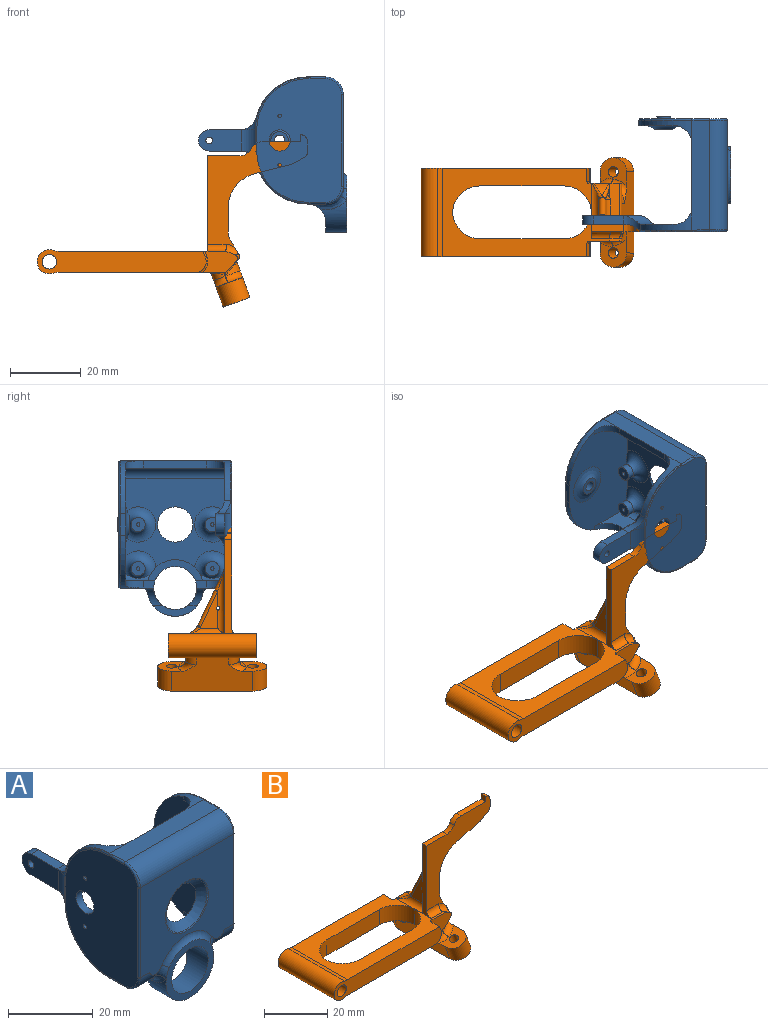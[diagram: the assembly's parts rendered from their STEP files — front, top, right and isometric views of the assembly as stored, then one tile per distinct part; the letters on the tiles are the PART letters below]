
ASSEMBLY  parts=2 mates=1
PART A: 112 faces, bbox 37.6x43.4x49.7 mm
  f0: plane 34.28x22.36mm, normal (1,0,0), area 579.8mm2, adj f18,f21,f30,f32,f33,f34,f36,f37
  f1: cylinder r=5mm len=6.53mm, axis (1,0,0), area 41.7mm2, adj f8,f9,f23,f66,f86,f87
  f2: cylinder r=5mm len=0.6mm, axis (1,0,0), area 0.1mm2, adj f9,f39,f89
  f3: plane 7.91x5.41mm, normal (0,0,-1), area 34.3mm2, adj f6,f20,f28,f70,f90
  f4: plane 3.24x2mm, normal (0,1,0), area 6mm2, adj f23,f30,f36,f80,f92
  f5: plane 10x8.24mm, normal (0,0,1), area 46.6mm2, adj f7,f28,f31,f35,f80,f82
  f6: cylinder r=5mm len=6.53mm, axis (1,0,0), area 41.7mm2, adj f3,f9,f39,f68,f89,f90
  f7: cylinder r=3mm len=6.99mm, axis (1,0,0), area 18.7mm2, adj f5,f31,f53,f81
  f8: cylinder r=2mm len=3.87mm, axis (0,1,0), area 0.6mm2, adj f1,f9,f44,f87
  f9: plane 31x27.5mm, normal (0,-1,0), area 595.5mm2, adj f1,f2,f6,f8,f27,f39,f44,f55
  f10: plane 1x1mm, normal (0,1,0), area 0.8mm2, adj f43
  f11: cylinder r=0.5mm len=5mm, axis (0,1,0), area 15.7mm2, adj f13,f40
  f12: cylinder r=2mm len=4mm, axis (0,1,0), area 25.1mm2, adj f13,f52
  f13: plane 4x4mm, normal (0,1,0), area 11.8mm2, adj f11,f12
  f14: plane 1x1mm, normal (0,1,0), area 0.8mm2, adj f17
  f15: cylinder r=2mm len=4mm, axis (0,1,0), area 25.1mm2, adj f16,f53
  f16: plane 4x4mm, normal (0,1,0), area 11.8mm2, adj f15,f17
  f17: cylinder r=0.5mm len=5mm, axis (0,1,0), area 15.7mm2, adj f14,f16
  f18: cylinder r=15mm len=14.52mm, axis (1,0,0), area 38.7mm2, adj f0,f25,f37,f97,f102,f103
  f19: cylinder r=15mm len=15mm, axis (1,0,0), area 40.7mm2, adj f25,f26,f31,f38,f73
  f20: cylinder r=15mm len=15mm, axis (-1,0,0), area 40.7mm2, adj f3,f26,f31,f35,f72
  f21: cylinder r=15mm len=14.52mm, axis (-1,0,0), area 38.7mm2, adj f0,f23,f36,f99,f100,f101
  f22: plane 35x24mm, normal (-1,0,0), area 711.2mm2, adj f56,f57,f58,f59,f60,f61,f62,f63
  f23: plane 8.1x5.41mm, normal (0,0,-1), area 34.6mm2, adj f1,f4,f21,f64,f86,f99
  f24: plane 35x24mm, normal (1,0,0), area 728.5mm2, adj f67,f68,f69,f70,f71,f72,f73,f74
  f25: plane 31.21x5.03mm, normal (0,0,1), area 155.3mm2, adj f18,f19,f27,f29,f61,f71,f97
  f26: plane 6x1.5mm, normal (0,1,0), area 9mm2, adj f19,f20,f31,f74
  f27: cylinder r=5mm len=31mm, axis (-1,0,0), area 243.5mm2, adj f9,f25,f63,f69
  f28: plane 3.24x2mm, normal (0,1,0), area 6mm2, adj f3,f5,f35,f80,f91
  f29: plane 18x2mm, normal (0,1,0), area 36mm2, adj f25,f32,f37,f38
  f30: plane 10x8.24mm, normal (0,0,1), area 46.6mm2, adj f0,f4,f36,f45,f80,f82
  f31: plane 34.28x23mm, normal (-1,0,0), area 580.8mm2, adj f5,f7,f19,f20,f26,f32,f33,f34
  f32: plane 28x10mm, normal (0,0,-1), area 150.7mm2, adj f0,f29,f31,f34,f37,f38
  f33: plane 28x25.2mm, normal (0,1,0), area 402mm2, adj f0,f31,f34,f50,f51,f52,f53,f54
  f34: cylinder r=3mm len=28mm, axis (-1,0,0), area 131.9mm2, adj f0,f31,f32,f33
  f35: cylinder r=5mm len=5mm, axis (0,0,-1), area 12.3mm2, adj f5,f20,f28,f31
  f36: cylinder r=5mm len=5mm, axis (0,0,1), area 12.3mm2, adj f0,f4,f21,f30
  f37: cylinder r=5mm len=5mm, axis (0,0,1), area 12.3mm2, adj f0,f18,f29,f32
  f38: cylinder r=5mm len=5mm, axis (0,0,-1), area 12.3mm2, adj f19,f29,f31,f32
  f39: cylinder r=2mm len=3.87mm, axis (0,1,0), area 0.6mm2, adj f2,f6,f9,f89
  f40: plane 1x1mm, normal (0,1,0), area 0.8mm2, adj f11
  f41: plane 4x4mm, normal (0,1,0), area 11.8mm2, adj f42,f43
  f42: cylinder r=2mm len=4mm, axis (0,1,0), area 25.1mm2, adj f41,f51
  f43: cylinder r=0.5mm len=5mm, axis (0,1,0), area 15.7mm2, adj f10,f41
  f44: cylinder r=5mm len=0.6mm, axis (1,0,0), area 0.1mm2, adj f8,f9,f87
  f45: cylinder r=3mm len=6.99mm, axis (1,0,0), area 18.7mm2, adj f0,f30,f50,f81
  f46: cylinder r=0.5mm len=5mm, axis (0,1,0), area 15.7mm2, adj f47,f49
  f47: plane 4x4mm, normal (0,1,0), area 11.8mm2, adj f46,f48
  f48: cylinder r=2mm len=4mm, axis (0,1,0), area 25.1mm2, adj f47,f50
  f49: plane 1x1mm, normal (0,1,0), area 0.8mm2, adj f46
  f50: torus R=5mm, axis (0,-1,0), area 66.5mm2, adj f0,f33,f45,f48,f81
  f51: torus R=5mm, axis (0,-1,0), area 83.9mm2, adj f0,f33,f42
  f52: torus R=5mm, axis (0,-1,0), area 83.9mm2, adj f12,f31,f33
  f53: torus R=5mm, axis (0,-1,0), area 66.5mm2, adj f7,f15,f31,f33,f81
  f54: cone r=5mm half-angle=45deg, axis (0,-1,0), area 97.6mm2, adj f33,f55
  f55: torus R=7.21mm, axis (0,-1,0), area 17.3mm2, adj f9,f54
  f56: cylinder r=3mm len=6mm, axis (-1,0,0), area 37.7mm2, adj f0,f22,f107
  f57: cylinder r=0.5mm len=2mm, axis (-1,0,0), area 6.3mm2, adj f0,f22
  f58: cylinder r=0.5mm len=2mm, axis (-1,0,0), area 6.3mm2, adj f0,f22
  f59: torus R=14.5mm, axis (1,0,0), area 10.2mm2, adj f22,f60,f61,f97
  f60: cylinder r=0.5mm len=6mm, axis (0,0,1), area 2.6mm2, adj f22,f59,f62,f98
  f61: cylinder r=0.5mm len=5mm, axis (0,-1,0), area 3.5mm2, adj f22,f25,f59,f63,f97
  f62: torus R=14.5mm, axis (1,0,0), area 10.2mm2, adj f22,f60,f64,f99
  f63: torus R=4.5mm, axis (1,0,0), area 5.9mm2, adj f22,f27,f61,f65
  f64: cylinder r=0.5mm len=5mm, axis (0,1,0), area 3.5mm2, adj f22,f23,f62,f66,f99
  f65: cylinder r=0.5mm len=26mm, axis (0,0,-1), area 20.4mm2, adj f9,f22,f63,f66
  f66: torus R=4.5mm, axis (1,0,0), area 5.9mm2, adj f1,f22,f64,f65
  f67: cylinder r=0.5mm len=26mm, axis (0,0,1), area 20.4mm2, adj f9,f24,f68,f69
  f68: torus R=4.5mm, axis (1,0,0), area 5.9mm2, adj f6,f24,f67,f70
  f69: torus R=4.5mm, axis (1,0,0), area 5.9mm2, adj f24,f27,f67,f71
  f70: cylinder r=0.5mm len=5mm, axis (0,-1,0), area 3.9mm2, adj f3,f24,f68,f72
  f71: cylinder r=0.5mm len=5mm, axis (0,1,0), area 3.9mm2, adj f24,f25,f69,f73
  f72: torus R=14.5mm, axis (1,0,0), area 18.3mm2, adj f20,f24,f70,f74
  f73: torus R=14.5mm, axis (1,0,0), area 18.3mm2, adj f19,f24,f71,f74
  f74: cylinder r=0.5mm len=6mm, axis (0,0,-1), area 4.7mm2, adj f24,f26,f72,f73
  f75: cylinder r=1.5mm len=3.5mm, axis (1,0,0), area 33mm2, adj f76,f79
  f76: plane 5x5mm, normal (-1,0,0), area 12.6mm2, adj f75,f77
  f77: torus R=5.5mm, axis (1,0,0), area 79.8mm2, adj f31,f76
  f78: cylinder r=2mm len=4mm, axis (-1,0,0), area 6.3mm2, adj f24,f79
  f79: plane 4x4mm, normal (1,0,0), area 5.5mm2, adj f75,f78
  f80: cylinder r=6.1mm len=12.2mm, axis (0,-1,0), area 261.4mm2, adj f4,f5,f28,f30,f82,f83,f84,f91
  f81: cylinder r=8mm len=15.49mm, axis (0,-1,0), area 56.2mm2, adj f7,f33,f45,f50,f53,f82
  f82: plane 15.49x6mm, normal (0,1,0), area 34.4mm2, adj f5,f30,f80,f81
  f83: plane 12.49x3mm, normal (0,1,0), area 20.9mm2, adj f80,f85,f91,f92
  f84: plane 16.13x16.13mm, normal (0,-1,0), area 84.2mm2, adj f80,f85,f87,f88,f89
  f85: cylinder r=8mm len=16mm, axis (0,-1,0), area 146.5mm2, adj f83,f84,f86,f90,f91,f92
  f86: bspline ~11.94x4.3mm, area 23.5mm2, adj f1,f23,f85,f87,f92
  f87: bspline ~4.41x3.22mm, area 7.4mm2, adj f1,f8,f44,f84,f86,f88
  f88: torus R=9.73mm, axis (0,-1,0), area 37.9mm2, adj f9,f84,f87,f89
  f89: bspline ~4.41x3.22mm, area 7.4mm2, adj f2,f6,f39,f84,f88,f90
  f90: bspline ~11.94x4.3mm, area 23.5mm2, adj f3,f6,f85,f89,f91
  f91: cylinder r=5mm len=5mm, axis (-1,0,0), area 15.1mm2, adj f28,f80,f83,f85,f90
  f92: cylinder r=5mm len=5mm, axis (1,0,0), area 15.1mm2, adj f4,f80,f83,f85,f86
  f93: plane 12.26x6.08mm, normal (-1,0,0), area 66.9mm2, adj f94,f95,f97,f98,f99,f101,f103,f104
  f94: plane 8.64x2.5mm, normal (0,0,1), area 21.6mm2, adj f93,f96,f103,f104
  f95: plane 8.64x2.5mm, normal (0,0,-1), area 21.6mm2, adj f93,f96,f101,f104
  f96: plane 15.91x6mm, normal (1,0,0), area 88.5mm2, adj f94,f95,f100,f102,f104,f105,f109,f110
  f97: torus R=18.74mm, axis (1,0,0), area 8.6mm2, adj f18,f25,f59,f61,f93,f98,f103
  f98: cylinder r=5mm len=6mm, axis (0,0,1), area 26.4mm2, adj f60,f93,f97,f99
  f99: torus R=18.74mm, axis (1,0,0), area 8.6mm2, adj f21,f23,f62,f64,f93,f98,f101
  f100: cylinder r=5mm len=9.15mm, axis (0,1,0), area 21.2mm2, adj f0,f21,f96,f101,f106,f109
  f101: cylinder r=5mm len=4.84mm, axis (-1,0,0), area 13.4mm2, adj f21,f93,f95,f99,f100
  f102: cylinder r=5mm len=9.15mm, axis (0,1,0), area 21.2mm2, adj f0,f18,f96,f103,f108,f111
  f103: cylinder r=5mm len=4.84mm, axis (1,0,0), area 13.4mm2, adj f18,f93,f94,f97,f102
  f104: cylinder r=3mm len=6mm, axis (1,0,0), area 23.6mm2, adj f93,f94,f95,f96
  f105: cylinder r=0.95mm len=2.5mm, axis (1,0,0), area 14.9mm2, adj f93,f96
  f106: cylinder r=2mm len=5.31mm, axis (0,0,-1), area 7.4mm2, adj f0,f100,f107,f109
  f107: bspline ~4.04x1.79mm, area 6.3mm2, adj f56,f106,f108,f110
  f108: cylinder r=2mm len=5.31mm, axis (0,0,-1), area 7.4mm2, adj f0,f102,f107,f111
  f109: cylinder r=4mm len=3.25mm, axis (0,0,-1), area 6.7mm2, adj f96,f100,f106,f110
  f110: bspline ~4.15x3.36mm, area 15.7mm2, adj f96,f107,f109,f111
  f111: cylinder r=4mm len=3.25mm, axis (0,0,-1), area 6.7mm2, adj f96,f102,f108,f110
PART B: 112 faces, bbox 77.3x31.7x49.5 mm
  f0: plane 31.86x28.29mm, normal (0,-1,0), area 315.2mm2, adj f2,f25,f29,f30,f31,f36,f37,f100
  f1: plane 28.29x20.74mm, normal (0,1,0), area 208.4mm2, adj f2,f25,f30,f35,f100,f101,f102,f103
  f2: plane 9.12x2mm, normal (0,0,1), area 18.2mm2, adj f0,f1,f25,f109
  f3: plane 4.14x3.26mm, normal (0.72,0,-0.69), area 6.9mm2, adj f4,f14,f68,f88,f90
  f4: plane 47.51x25.12mm, normal (0,0,-1), area 506.8mm2, adj f3,f6,f8,f18,f19,f20,f21,f22
  f5: plane 47.47x25.08mm, normal (0,0,1), area 512.4mm2, adj f6,f10,f16,f18,f19,f20,f21,f22
  f6: plane 47.87x6.83mm, normal (0,-1,0), area 269.8mm2, adj f4,f5,f17,f70,f72,f97,f98,f99
  f7: plane 0.72x0.1mm, normal (0,0,1), area 0mm2, adj f9,f12,f68
  f8: plane 5.59x3.78mm, normal (0.72,0,-0.69), area 9mm2, adj f4,f64,f65,f66,f67,f71,f78,f79
  f9: plane 9.73x2.8mm, normal (0.37,0,0.93), area 28.5mm2, adj f7,f14,f33,f45,f47,f48,f68
  f10: cylinder r=2mm len=11.73mm, axis (0,-1,0), area 26.6mm2, adj f5,f13,f26,f34,f68
  f11: cylinder r=5mm len=4.5mm, axis (-1,0,0), area 8.4mm2, adj f12,f13,f43,f68
  f12: bspline ~5.19x2.89mm, area 4.8mm2, adj f7,f11,f33,f43,f48,f68
  f13: bspline ~4.84x2.8mm, area 4.7mm2, adj f10,f11,f43,f68
  f14: cylinder r=1mm len=9.73mm, axis (0,-1,0), area 18.2mm2, adj f3,f9,f67,f68,f84,f86
  f15: plane 3.06x1.63mm, normal (0,1,0), area 1.8mm2, adj f29,f31,f32,f45
  f16: plane 2.79x1.13mm, normal (0.37,0,0.93), area 2.2mm2, adj f5,f37,f64,f71
  f17: cylinder r=2.05mm len=25mm, axis (0,1,0), area 322mm2, adj f6,f18
  f18: plane 47.87x6.83mm, normal (0,1,0), area 269.8mm2, adj f4,f5,f17,f69,f73,f97,f98,f99
  f19: plane 23.48x6mm, normal (0,1,0), area 140.9mm2, adj f4,f5,f22,f23
  f20: plane 23.48x6mm, normal (0,-1,0), area 140.9mm2, adj f4,f5,f21,f24
  f21: cylinder r=8mm len=7.98mm, axis (0,0,-1), area 72.4mm2, adj f4,f5,f20,f22
  f22: cylinder r=8mm len=7.98mm, axis (0,0,1), area 72.4mm2, adj f4,f5,f19,f21
  f23: cylinder r=8mm len=7.98mm, axis (0,0,-1), area 72.4mm2, adj f4,f5,f19,f24
  f24: cylinder r=8mm len=7.98mm, axis (0,0,1), area 72.4mm2, adj f4,f5,f20,f23
  f25: plane 27x4mm, normal (-1,0,0), area 54.9mm2, adj f0,f1,f2,f5,f34,f36
  f26: plane 10.37x4.96mm, normal (-1,0,0), area 25.3mm2, adj f10,f34,f41,f43,f44
  f27: plane 10.57x5.08mm, normal (1,0,0), area 26.3mm2, adj f32,f41,f43,f44,f47
  f28: plane 5.08x2.45mm, normal (0,0.9,0.43), area 4.1mm2, adj f35,f39,f42
  f29: plane 4.22x3.13mm, normal (0.86,0,0.51), area 10.6mm2, adj f0,f15,f31,f37,f45,f65,f66,f67
  f30: plane 14.42x2.03mm, normal (1,0,0), area 13.4mm2, adj f0,f1,f31,f32,f35,f38,f102
  f31: cylinder r=5mm len=2.53mm, axis (0,-1,0), area 5.3mm2, adj f0,f15,f29,f30,f32
  f32: cylinder r=2mm len=17.78mm, axis (0,0,-1), area 42.4mm2, adj f15,f27,f30,f31,f38,f39,f44,f46
  f33: cylinder r=2mm len=2.93mm, axis (0,-1,0), area 0.6mm2, adj f9,f12,f48
  f34: cylinder r=2mm len=20.03mm, axis (0,0,1), area 48mm2, adj f10,f25,f26,f40,f42,f44
  f35: cylinder r=5mm len=5.79mm, axis (1,0,0), area 9.3mm2, adj f1,f28,f30,f38,f40
  f36: cylinder r=2mm len=5.51mm, axis (-1,0,0), area 16.7mm2, adj f0,f5,f25,f37
  f37: cylinder r=2mm len=4.34mm, axis (-0.93,0,0.37), area 10.1mm2, adj f0,f16,f29,f36,f65
  f38: bspline ~2.7x1.86mm, area 1mm2, adj f30,f32,f35,f39
  f39: bspline ~7.12x3.2mm, area 6.6mm2, adj f28,f32,f38,f41
  f40: bspline ~2.71x1.86mm, area 0.7mm2, adj f34,f35,f42
  f41: cylinder r=1mm len=10.38mm, axis (0,-0.43,0.9), area 34.6mm2, adj f26,f27,f39,f42,f43
  f42: bspline ~7.12x3.2mm, area 6.6mm2, adj f28,f34,f40,f41
  f43: torus R=6mm, axis (1,0,0), area 1.7mm2, adj f11,f12,f13,f26,f27,f41,f48
  f44: cylinder r=0.5mm len=2mm, axis (-1,0,0), area 6.3mm2, adj f26,f27,f32,f34
  f45: cylinder r=2mm len=3.85mm, axis (0.93,0,-0.37), area 9mm2, adj f9,f15,f29,f46,f67
  f46: sphere r=2mm, area 5.1mm2, adj f32,f45,f47
  f47: cylinder r=2mm len=5.08mm, axis (0,1,0), area 12.1mm2, adj f9,f27,f46,f48
  f48: bspline ~2.43x1.86mm, area 2.2mm2, adj f9,f12,f33,f43,f47
  f49: cylinder r=4mm len=9.57mm, axis (-0.34,0,0.94), area 75.4mm2, adj f51,f52,f57,f59
  f50: cylinder r=1.5mm len=6.66mm, axis (-0.34,0,0.94), area 56.5mm2, adj f51,f52
  f51: plane 31x7.52mm, normal (0.34,0,-0.94), area 220.1mm2, adj f49,f50,f54,f55,f57,f59
  f52: plane 8.05x7.52mm, normal (-0.34,0,0.94), area 37.8mm2, adj f49,f50,f57,f59,f91,f92,f93
  f53: cylinder r=4mm len=0.65mm, axis (0.34,0,-0.94), area 0.1mm2, adj f60,f62,f89,f92
  f54: cylinder r=4mm len=9.57mm, axis (-0.34,0,0.94), area 75.4mm2, adj f51,f56,f57,f59
  f55: cylinder r=1.5mm len=6.66mm, axis (-0.34,0,0.94), area 56.5mm2, adj f51,f56
  f56: plane 8.05x7.52mm, normal (-0.34,0,0.94), area 37.8mm2, adj f54,f55,f57,f59,f94,f95,f96
  f57: plane 23.58x10.6mm, normal (0.94,0,0.34), area 169mm2, adj f49,f51,f52,f54,f56,f62,f63,f82
  f58: cylinder r=4mm len=0.65mm, axis (0.34,0,-0.94), area 0.1mm2, adj f61,f63,f81,f95
  f59: plane 23.68x10.17mm, normal (-0.94,0,-0.34), area 181.3mm2, adj f49,f51,f52,f54,f56,f60,f61,f85
  f60: cylinder r=3mm len=3.94mm, axis (0.34,0,-0.94), area 7.1mm2, adj f53,f59,f87,f93
  f61: cylinder r=3mm len=3.94mm, axis (0.34,0,-0.94), area 7.1mm2, adj f58,f59,f83,f94
  f62: cylinder r=5mm len=5.09mm, axis (0.34,0,-0.94), area 13.1mm2, adj f53,f57,f86,f88,f90,f91
  f63: cylinder r=5mm len=5.08mm, axis (0.34,0,-0.94), area 13.1mm2, adj f57,f58,f78,f79,f80,f96
  f64: cylinder r=1mm len=1.62mm, axis (0,-1,0), area 1.4mm2, adj f8,f16,f65,f71
  f65: bspline ~2.46x2.22mm, area 3.5mm2, adj f8,f29,f37,f64,f66
  f66: cylinder r=1mm len=3.02mm, axis (0,1,0), area 3.4mm2, adj f8,f29,f65,f67
  f67: bspline ~2.98x2.22mm, area 3.3mm2, adj f8,f14,f29,f45,f66,f80,f82
  f68: plane 10.17x6.03mm, normal (0,1,0), area 44.9mm2, adj f3,f4,f5,f7,f9,f10,f11,f12
  f69: plane 3.77x1.97mm, normal (0.94,0,0.34), area 7.9mm2, adj f5,f18,f73,f76
  f70: plane 3.77x1.97mm, normal (0.94,0,0.34), area 7.9mm2, adj f5,f6,f72,f74
  f71: plane 10.16x6mm, normal (0,-1,0), area 44.8mm2, adj f4,f5,f8,f16,f64,f74,f75
  f72: cylinder r=3mm len=4.03mm, axis (0,-1,0), area 21.7mm2, adj f4,f6,f70,f75
  f73: cylinder r=3mm len=4.03mm, axis (0,-1,0), area 21.7mm2, adj f4,f18,f69,f77
  f74: cylinder r=0.5mm len=2.15mm, axis (0.34,0,-0.94), area 1.6mm2, adj f5,f70,f71,f75
  f75: torus R=3.5mm, axis (0,1,0), area 4.1mm2, adj f4,f71,f72,f74
  f76: cylinder r=0.5mm len=2.15mm, axis (0.34,0,-0.94), area 1.6mm2, adj f5,f68,f69,f77
  f77: torus R=3.5mm, axis (0,1,0), area 4.1mm2, adj f4,f68,f73,f76
  f78: bspline ~5.32x3.96mm, area 4.7mm2, adj f8,f63,f79,f80
  f79: bspline ~0.55x0.53mm, area 0.2mm2, adj f4,f8,f63,f78,f81
  f80: bspline ~0.52x0.29mm, area 0mm2, adj f63,f67,f78,f82
  f81: bspline ~0.52x0.51mm, area 0.1mm2, adj f4,f58,f79,f83
  f82: bspline ~2.54x0.64mm, area 0.5mm2, adj f57,f67,f80,f84
  f83: bspline ~4.26x3.5mm, area 3.9mm2, adj f4,f61,f81,f85
  f84: cylinder r=0.5mm len=4.05mm, axis (0,-1,0), area 1.9mm2, adj f14,f57,f82,f86
  f85: cylinder r=0.5mm len=9.14mm, axis (0,1,0), area 5.6mm2, adj f4,f59,f83,f87
  f86: bspline ~3.49x0.88mm, area 0.7mm2, adj f14,f62,f84,f88
  f87: bspline ~4.26x3.5mm, area 3.9mm2, adj f4,f60,f85,f89
  f88: bspline ~4x3.78mm, area 3.9mm2, adj f3,f62,f86,f90
  f89: bspline ~0.52x0.51mm, area 0.1mm2, adj f4,f53,f87,f90
  f90: bspline ~0.55x0.53mm, area 0.2mm2, adj f3,f4,f62,f88,f89
  f91: torus R=7mm, axis (-0.34,0,0.94), area 18.9mm2, adj f52,f57,f62,f92
  f92: torus R=2mm, axis (-0.34,0,0.94), area 0.3mm2, adj f52,f53,f91,f93
  f93: torus R=5mm, axis (-0.34,0,0.94), area 14.1mm2, adj f52,f59,f60,f92
  f94: torus R=5mm, axis (-0.34,0,0.94), area 14.1mm2, adj f56,f59,f61,f95
  f95: torus R=2mm, axis (-0.34,0,0.94), area 0.3mm2, adj f56,f58,f94,f96
  f96: torus R=7mm, axis (-0.34,0,0.94), area 18.9mm2, adj f56,f57,f63,f95
  f97: cylinder r=3.41mm len=25mm, axis (0,-1,0), area 321.9mm2, adj f6,f18,f98,f99
  f98: cylinder r=5mm len=25mm, axis (0,-1,0), area 39.4mm2, adj f4,f6,f18,f97
  f99: cylinder r=5mm len=25mm, axis (0,-1,0), area 39.4mm2, adj f5,f6,f18,f97
  f100: plane 2x0.13mm, normal (-0.89,0,0.45), area 0.3mm2, adj f0,f1,f108,f109
  f101: plane 10.23x2.61mm, normal (0.25,0,-0.97), area 21.1mm2, adj f0,f1,f102,f107
  f102: cylinder r=10mm len=9.69mm, axis (0,-1,0), area 26.4mm2, adj f0,f1,f30,f101
  f103: plane 10.84x2mm, normal (0,0,1), area 21.7mm2, adj f0,f1,f108,f110
  f104: plane 2.8x2mm, normal (1,0,0), area 5.6mm2, adj f0,f1,f106,f111
  f105: plane 3.23x2mm, normal (0.47,0,-0.88), area 7.3mm2, adj f0,f1,f106,f107
  f106: cylinder r=2mm len=2mm, axis (0,1,0), area 4.3mm2, adj f0,f1,f104,f105
  f107: cylinder r=2mm len=2mm, axis (0,-1,0), area 0.9mm2, adj f0,f1,f101,f105
  f108: cylinder r=3.5mm len=3.13mm, axis (0,-1,0), area 7.8mm2, adj f0,f1,f100,f103
  f109: cylinder r=3.5mm len=3.13mm, axis (0,-1,0), area 7.8mm2, adj f0,f1,f2,f100
  f110: plane 2x2mm, normal (-1,0,0), area 4mm2, adj f0,f1,f103,f111
  f111: cylinder r=2mm len=2mm, axis (0,1,0), area 6.3mm2, adj f0,f1,f104,f110
PLACE A rot(axis=(0,0,1),90deg) t=(182.03,-15.1,88.64)mm
PLACE B t=(105.74,-13.11,60.52)mm
MATE parallel A.f93 <-> B.f1  axis (0,-1,0) through (154.61,-29.1,94.89)mm
